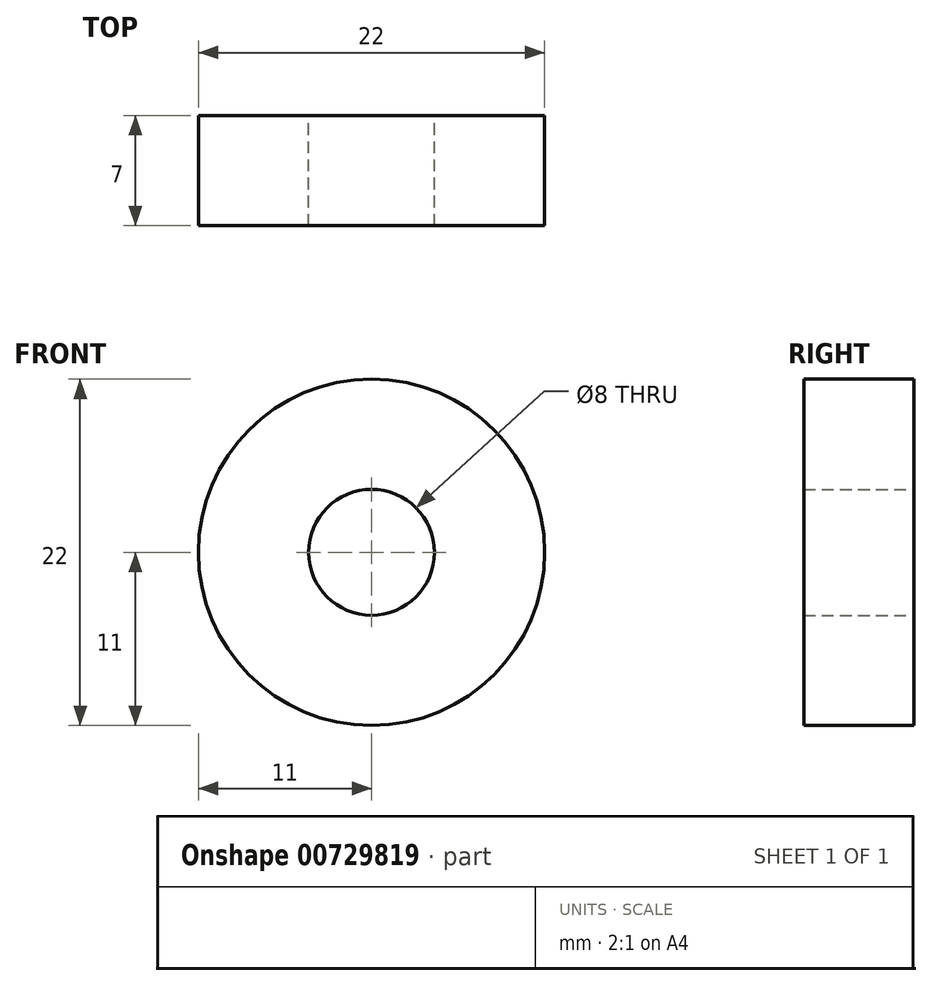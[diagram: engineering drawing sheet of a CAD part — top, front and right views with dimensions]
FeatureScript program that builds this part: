
annotation { "Feature Type Name" : "Feature", "Feature Type Description" : "" }
export const myFeature = defineFeature(function(context is Context, id is Id, definition is map)
    precondition{}
    {
        {
            var Q0;
            Q0=qCreatedBy(makeId("Front.planeOp"),FACE);
            var sketch = newSketch(context, id + "F0", { "sketchPlane" : qUnion([Q0])});
            skCircle(sketch, "E0", {"center": v(0, 0) * mm, "radius": 11 * mm});
            skCircle(sketch, "E1", {"center": v(0, 0) * mm, "radius": 4 * mm});
            skSolve(sketch);
        }
        {
            var Q0;
            Q0 = qSketchRegion(id + "F0", true);
            extrude(context, id + "F1", {"entities" : qUnion([Q0]), "depth" : 7 * mm, "offsetDistance" : 25 * mm});
        }
    });
